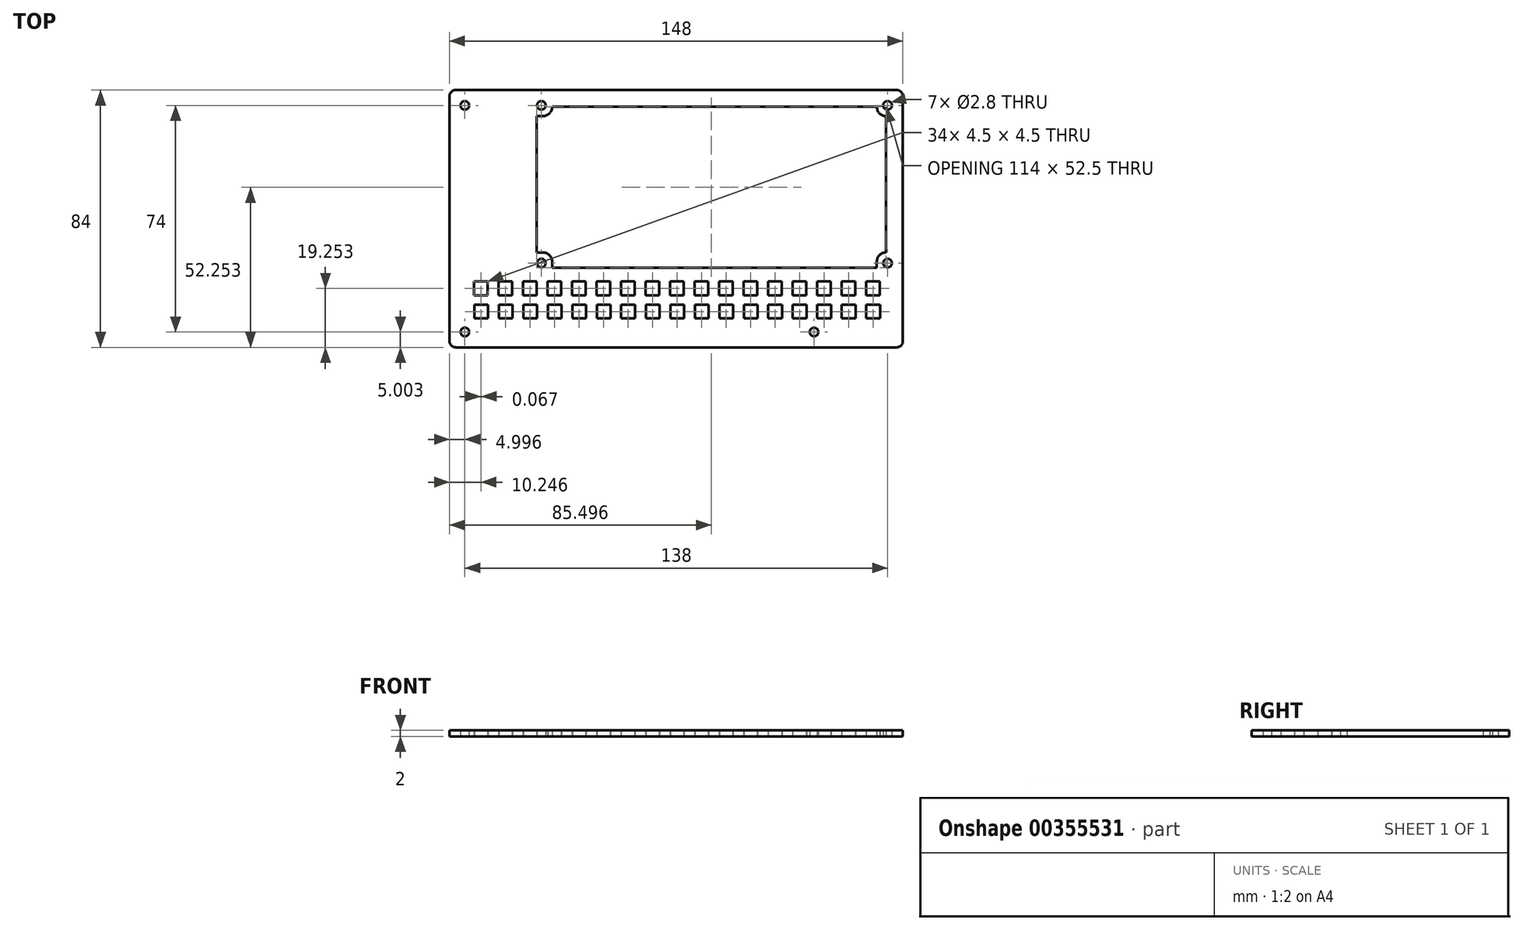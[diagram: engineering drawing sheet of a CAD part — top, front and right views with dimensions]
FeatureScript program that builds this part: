
annotation { "Feature Type Name" : "Feature", "Feature Type Description" : "" }
export const myFeature = defineFeature(function(context is Context, id is Id, definition is map)
    precondition{}
    {
        {
            var Q0;
            Q0=qCreatedBy(makeId("Top.planeOp"),FACE);
            var sketch = newSketch(context, id + "F0", { "sketchPlane" : qUnion([Q0])});
            skLineSegment(sketch, "E0.bottom", {"start": v(-72.45, 22.86) * mm, "end": v(71.55, 22.86) * mm});
            skLineSegment(sketch, "E0.top", {"start": v(-72.45, -61.14) * mm, "end": v(71.55, -61.14) * mm});
            skLineSegment(sketch, "E0.left", {"start": v(-74.45, 20.86) * mm, "end": v(-74.45, -59.14) * mm});
            skLineSegment(sketch, "E0.right", {"start": v(73.55, 20.86) * mm, "end": v(73.55, -59.14) * mm});
            skPoint(sketch, "E1.visualSharp", {"position": v(-74.45, 22.86) * mm});
            skArc(sketch, "E1.filletArc", {"start": v(-72.45, 22.86) * mm, "mid": v(-73.87, 22.28) * mm, "end": v(-74.45, 20.86) * mm});
            skPoint(sketch, "E2.visualSharp", {"position": v(73.55, 22.86) * mm});
            skArc(sketch, "E2.filletArc", {"start": v(73.55, 20.86) * mm, "mid": v(72.96, 22.28) * mm, "end": v(71.55, 22.86) * mm});
            skPoint(sketch, "E3.visualSharp", {"position": v(73.55, -61.14) * mm});
            skArc(sketch, "E3.filletArc", {"start": v(71.55, -61.14) * mm, "mid": v(72.96, -60.55) * mm, "end": v(73.55, -59.14) * mm});
            skPoint(sketch, "E4.visualSharp", {"position": v(-74.45, -61.14) * mm});
            skArc(sketch, "E4.filletArc", {"start": v(-74.45, -59.14) * mm, "mid": v(-73.87, -60.55) * mm, "end": v(-72.45, -61.14) * mm});
            skCircle(sketch, "E5", {"center": v(-69.45, 17.86) * mm, "radius": 1.4 * mm});
            skCircle(sketch, "E6", {"center": v(68.55, 17.86) * mm, "radius": 1.4 * mm});
            skCircle(sketch, "E7", {"center": v(-44.45, 17.86) * mm, "radius": 1.4 * mm});
            skCircle(sketch, "E8", {"center": v(-44.45, -33.64) * mm, "radius": 1.4 * mm});
            skCircle(sketch, "E9", {"center": v(68.55, -33.64) * mm, "radius": 1.4 * mm});
            skCircle(sketch, "E10", {"center": v(-69.45, -56.14) * mm, "radius": 1.4 * mm});
            skCircle(sketch, "E11", {"center": v(44.55, -56.14) * mm, "radius": 1.4 * mm});
            skLineSegment(sketch, "E12.top", {"start": v(-45.95, 14.36) * mm, "end": v(-43.95, 14.36) * mm});
            skLineSegment(sketch, "E13.top", {"start": v(-45.95, -30.14) * mm, "end": v(-43.95, -30.14) * mm});
            skLineSegment(sketch, "E13.right", {"start": v(-40.95, -35.14) * mm, "end": v(-40.95, -33.14) * mm});
            skLineSegment(sketch, "E14.right", {"start": v(65.05, -35.14) * mm, "end": v(65.05, -33.14) * mm});
            skLineSegment(sketch, "E15", {"start": v(65.05, -35.14) * mm, "end": v(-40.95, -35.14) * mm});
            skLineSegment(sketch, "E16", {"start": v(-45.95, -30.14) * mm, "end": v(-45.95, 14.36) * mm});
            skPoint(sketch, "E17.visualSharp", {"position": v(-40.95, 14.36) * mm});
            skArc(sketch, "E17.filletArc", {"start": v(-43.95, 14.36) * mm, "mid": v(-41.83, 15.24) * mm, "end": v(-40.95, 17.36) * mm});
            skPoint(sketch, "E18.visualSharp", {"position": v(65.05, 14.36) * mm});
            skArc(sketch, "E18.filletArc", {"start": v(65.05, 17.36) * mm, "mid": v(65.92, 15.24) * mm, "end": v(68.05, 14.36) * mm});
            skPoint(sketch, "E19.visualSharp", {"position": v(65.05, -30.14) * mm});
            skArc(sketch, "E19.filletArc", {"start": v(68.05, -30.14) * mm, "mid": v(65.92, -31.02) * mm, "end": v(65.05, -33.14) * mm});
            skPoint(sketch, "E20.visualSharp", {"position": v(-40.95, -30.14) * mm});
            skArc(sketch, "E20.filletArc", {"start": v(-40.95, -33.14) * mm, "mid": v(-41.83, -31.02) * mm, "end": v(-43.95, -30.14) * mm});
            skLineSegment(sketch, "E21", {"start": v(68.05, 14.36) * mm, "end": v(68.05, -30.14) * mm});
            skLineSegment(sketch, "E22", {"start": v(65.05, 17.36) * mm, "end": v(-40.95, 17.36) * mm});
            skLineSegment(sketch, "E23.bottom", {"start": v(-66.45, -39.64) * mm, "end": v(-61.95, -39.64) * mm});
            skLineSegment(sketch, "E23.top", {"start": v(-66.45, -44.14) * mm, "end": v(-61.95, -44.14) * mm});
            skLineSegment(sketch, "E23.left", {"start": v(-66.45, -39.64) * mm, "end": v(-66.45, -44.14) * mm});
            skLineSegment(sketch, "E23.right", {"start": v(-61.95, -39.64) * mm, "end": v(-61.95, -44.14) * mm});
            skLineSegment(sketch, "E24.bottom", {"start": v(-66.39, -47.2) * mm, "end": v(-61.89, -47.2) * mm});
            skLineSegment(sketch, "E24.top", {"start": v(-66.39, -51.7) * mm, "end": v(-61.89, -51.7) * mm});
            skLineSegment(sketch, "E24.left", {"start": v(-66.39, -47.2) * mm, "end": v(-66.39, -51.7) * mm});
            skLineSegment(sketch, "E24.right", {"start": v(-61.89, -47.2) * mm, "end": v(-61.89, -51.7) * mm});
            skLineSegment(sketch, "E25.1.0.0", {"start": v(-53.89, -47.2) * mm, "end": v(-53.89, -51.7) * mm});
            skLineSegment(sketch, "E25.1.0.1", {"start": v(-58.39, -47.2) * mm, "end": v(-58.39, -51.7) * mm});
            skLineSegment(sketch, "E25.1.0.2", {"start": v(-58.39, -51.7) * mm, "end": v(-53.89, -51.7) * mm});
            skLineSegment(sketch, "E25.1.0.3", {"start": v(-58.39, -47.2) * mm, "end": v(-53.89, -47.2) * mm});
            skLineSegment(sketch, "E25.1.0.4", {"start": v(-53.95, -39.64) * mm, "end": v(-53.95, -44.14) * mm});
            skLineSegment(sketch, "E25.1.0.5", {"start": v(-58.45, -44.14) * mm, "end": v(-53.95, -44.14) * mm});
            skLineSegment(sketch, "E25.1.0.6", {"start": v(-58.45, -39.64) * mm, "end": v(-58.45, -44.14) * mm});
            skLineSegment(sketch, "E25.1.0.7", {"start": v(-58.45, -39.64) * mm, "end": v(-53.95, -39.64) * mm});
            skLineSegment(sketch, "E25.2.0.0", {"start": v(-45.89, -47.2) * mm, "end": v(-45.89, -51.7) * mm});
            skLineSegment(sketch, "E25.2.0.1", {"start": v(-50.39, -47.2) * mm, "end": v(-50.39, -51.7) * mm});
            skLineSegment(sketch, "E25.2.0.2", {"start": v(-50.39, -51.7) * mm, "end": v(-45.89, -51.7) * mm});
            skLineSegment(sketch, "E25.2.0.3", {"start": v(-50.39, -47.2) * mm, "end": v(-45.89, -47.2) * mm});
            skLineSegment(sketch, "E25.2.0.4", {"start": v(-45.95, -39.64) * mm, "end": v(-45.95, -44.14) * mm});
            skLineSegment(sketch, "E25.2.0.5", {"start": v(-50.45, -44.14) * mm, "end": v(-45.95, -44.14) * mm});
            skLineSegment(sketch, "E25.2.0.6", {"start": v(-50.45, -39.64) * mm, "end": v(-50.45, -44.14) * mm});
            skLineSegment(sketch, "E25.2.0.7", {"start": v(-50.45, -39.64) * mm, "end": v(-45.95, -39.64) * mm});
            skLineSegment(sketch, "E25.3.0.0", {"start": v(-37.89, -47.2) * mm, "end": v(-37.89, -51.7) * mm});
            skLineSegment(sketch, "E25.3.0.1", {"start": v(-42.39, -47.2) * mm, "end": v(-42.39, -51.7) * mm});
            skLineSegment(sketch, "E25.3.0.2", {"start": v(-42.39, -51.7) * mm, "end": v(-37.89, -51.7) * mm});
            skLineSegment(sketch, "E25.3.0.3", {"start": v(-42.39, -47.2) * mm, "end": v(-37.89, -47.2) * mm});
            skLineSegment(sketch, "E25.3.0.4", {"start": v(-37.95, -39.64) * mm, "end": v(-37.95, -44.14) * mm});
            skLineSegment(sketch, "E25.3.0.5", {"start": v(-42.45, -44.14) * mm, "end": v(-37.95, -44.14) * mm});
            skLineSegment(sketch, "E25.3.0.6", {"start": v(-42.45, -39.64) * mm, "end": v(-42.45, -44.14) * mm});
            skLineSegment(sketch, "E25.3.0.7", {"start": v(-42.45, -39.64) * mm, "end": v(-37.95, -39.64) * mm});
            skLineSegment(sketch, "E25.4.0.0", {"start": v(-29.89, -47.2) * mm, "end": v(-29.89, -51.7) * mm});
            skLineSegment(sketch, "E25.4.0.1", {"start": v(-34.39, -47.2) * mm, "end": v(-34.39, -51.7) * mm});
            skLineSegment(sketch, "E25.4.0.2", {"start": v(-34.39, -51.7) * mm, "end": v(-29.89, -51.7) * mm});
            skLineSegment(sketch, "E25.4.0.3", {"start": v(-34.39, -47.2) * mm, "end": v(-29.89, -47.2) * mm});
            skLineSegment(sketch, "E25.4.0.4", {"start": v(-29.95, -39.64) * mm, "end": v(-29.95, -44.14) * mm});
            skLineSegment(sketch, "E25.4.0.5", {"start": v(-34.45, -44.14) * mm, "end": v(-29.95, -44.14) * mm});
            skLineSegment(sketch, "E25.4.0.6", {"start": v(-34.45, -39.64) * mm, "end": v(-34.45, -44.14) * mm});
            skLineSegment(sketch, "E25.4.0.7", {"start": v(-34.45, -39.64) * mm, "end": v(-29.95, -39.64) * mm});
            skLineSegment(sketch, "E25.5.0.0", {"start": v(-21.89, -47.2) * mm, "end": v(-21.89, -51.7) * mm});
            skLineSegment(sketch, "E25.5.0.1", {"start": v(-26.39, -47.2) * mm, "end": v(-26.39, -51.7) * mm});
            skLineSegment(sketch, "E25.5.0.2", {"start": v(-26.39, -51.7) * mm, "end": v(-21.89, -51.7) * mm});
            skLineSegment(sketch, "E25.5.0.3", {"start": v(-26.39, -47.2) * mm, "end": v(-21.89, -47.2) * mm});
            skLineSegment(sketch, "E25.5.0.4", {"start": v(-21.95, -39.64) * mm, "end": v(-21.95, -44.14) * mm});
            skLineSegment(sketch, "E25.5.0.5", {"start": v(-26.45, -44.14) * mm, "end": v(-21.95, -44.14) * mm});
            skLineSegment(sketch, "E25.5.0.6", {"start": v(-26.45, -39.64) * mm, "end": v(-26.45, -44.14) * mm});
            skLineSegment(sketch, "E25.5.0.7", {"start": v(-26.45, -39.64) * mm, "end": v(-21.95, -39.64) * mm});
            skLineSegment(sketch, "E25.6.0.0", {"start": v(-13.89, -47.2) * mm, "end": v(-13.89, -51.7) * mm});
            skLineSegment(sketch, "E25.6.0.1", {"start": v(-18.39, -47.2) * mm, "end": v(-18.39, -51.7) * mm});
            skLineSegment(sketch, "E25.6.0.2", {"start": v(-18.39, -51.7) * mm, "end": v(-13.89, -51.7) * mm});
            skLineSegment(sketch, "E25.6.0.3", {"start": v(-18.39, -47.2) * mm, "end": v(-13.89, -47.2) * mm});
            skLineSegment(sketch, "E25.6.0.4", {"start": v(-13.95, -39.64) * mm, "end": v(-13.95, -44.14) * mm});
            skLineSegment(sketch, "E25.6.0.5", {"start": v(-18.45, -44.14) * mm, "end": v(-13.95, -44.14) * mm});
            skLineSegment(sketch, "E25.6.0.6", {"start": v(-18.45, -39.64) * mm, "end": v(-18.45, -44.14) * mm});
            skLineSegment(sketch, "E25.6.0.7", {"start": v(-18.45, -39.64) * mm, "end": v(-13.95, -39.64) * mm});
            skLineSegment(sketch, "E25.7.0.0", {"start": v(-5.89, -47.2) * mm, "end": v(-5.89, -51.7) * mm});
            skLineSegment(sketch, "E25.7.0.1", {"start": v(-10.39, -47.2) * mm, "end": v(-10.39, -51.7) * mm});
            skLineSegment(sketch, "E25.7.0.2", {"start": v(-10.39, -51.7) * mm, "end": v(-5.89, -51.7) * mm});
            skLineSegment(sketch, "E25.7.0.3", {"start": v(-10.39, -47.2) * mm, "end": v(-5.89, -47.2) * mm});
            skLineSegment(sketch, "E25.7.0.4", {"start": v(-5.95, -39.64) * mm, "end": v(-5.95, -44.14) * mm});
            skLineSegment(sketch, "E25.7.0.5", {"start": v(-10.45, -44.14) * mm, "end": v(-5.95, -44.14) * mm});
            skLineSegment(sketch, "E25.7.0.6", {"start": v(-10.45, -39.64) * mm, "end": v(-10.45, -44.14) * mm});
            skLineSegment(sketch, "E25.7.0.7", {"start": v(-10.45, -39.64) * mm, "end": v(-5.95, -39.64) * mm});
            skLineSegment(sketch, "E25.8.0.0", {"start": v(2.11, -47.2) * mm, "end": v(2.11, -51.7) * mm});
            skLineSegment(sketch, "E25.8.0.1", {"start": v(-2.39, -47.2) * mm, "end": v(-2.39, -51.7) * mm});
            skLineSegment(sketch, "E25.8.0.2", {"start": v(-2.39, -51.7) * mm, "end": v(2.11, -51.7) * mm});
            skLineSegment(sketch, "E25.8.0.3", {"start": v(-2.39, -47.2) * mm, "end": v(2.11, -47.2) * mm});
            skLineSegment(sketch, "E25.8.0.4", {"start": v(2.05, -39.64) * mm, "end": v(2.05, -44.14) * mm});
            skLineSegment(sketch, "E25.8.0.5", {"start": v(-2.45, -44.14) * mm, "end": v(2.05, -44.14) * mm});
            skLineSegment(sketch, "E25.8.0.6", {"start": v(-2.45, -39.64) * mm, "end": v(-2.45, -44.14) * mm});
            skLineSegment(sketch, "E25.8.0.7", {"start": v(-2.45, -39.64) * mm, "end": v(2.05, -39.64) * mm});
            skLineSegment(sketch, "E25.9.0.0", {"start": v(10.11, -47.2) * mm, "end": v(10.11, -51.7) * mm});
            skLineSegment(sketch, "E25.9.0.1", {"start": v(5.61, -47.2) * mm, "end": v(5.61, -51.7) * mm});
            skLineSegment(sketch, "E25.9.0.2", {"start": v(5.61, -51.7) * mm, "end": v(10.11, -51.7) * mm});
            skLineSegment(sketch, "E25.9.0.3", {"start": v(5.61, -47.2) * mm, "end": v(10.11, -47.2) * mm});
            skLineSegment(sketch, "E25.9.0.4", {"start": v(10.05, -39.64) * mm, "end": v(10.05, -44.14) * mm});
            skLineSegment(sketch, "E25.9.0.5", {"start": v(5.55, -44.14) * mm, "end": v(10.05, -44.14) * mm});
            skLineSegment(sketch, "E25.9.0.6", {"start": v(5.55, -39.64) * mm, "end": v(5.55, -44.14) * mm});
            skLineSegment(sketch, "E25.9.0.7", {"start": v(5.55, -39.64) * mm, "end": v(10.05, -39.64) * mm});
            skLineSegment(sketch, "E25.10.0.0", {"start": v(18.11, -47.2) * mm, "end": v(18.11, -51.7) * mm});
            skLineSegment(sketch, "E25.10.0.1", {"start": v(13.61, -47.2) * mm, "end": v(13.61, -51.7) * mm});
            skLineSegment(sketch, "E25.10.0.2", {"start": v(13.61, -51.7) * mm, "end": v(18.11, -51.7) * mm});
            skLineSegment(sketch, "E25.10.0.3", {"start": v(13.61, -47.2) * mm, "end": v(18.11, -47.2) * mm});
            skLineSegment(sketch, "E25.10.0.4", {"start": v(18.05, -39.64) * mm, "end": v(18.05, -44.14) * mm});
            skLineSegment(sketch, "E25.10.0.5", {"start": v(13.55, -44.14) * mm, "end": v(18.05, -44.14) * mm});
            skLineSegment(sketch, "E25.10.0.6", {"start": v(13.55, -39.64) * mm, "end": v(13.55, -44.14) * mm});
            skLineSegment(sketch, "E25.10.0.7", {"start": v(13.55, -39.64) * mm, "end": v(18.05, -39.64) * mm});
            skLineSegment(sketch, "E25.11.0.0", {"start": v(26.11, -47.2) * mm, "end": v(26.11, -51.7) * mm});
            skLineSegment(sketch, "E25.11.0.1", {"start": v(21.61, -47.2) * mm, "end": v(21.61, -51.7) * mm});
            skLineSegment(sketch, "E25.11.0.2", {"start": v(21.61, -51.7) * mm, "end": v(26.11, -51.7) * mm});
            skLineSegment(sketch, "E25.11.0.3", {"start": v(21.61, -47.2) * mm, "end": v(26.11, -47.2) * mm});
            skLineSegment(sketch, "E25.11.0.4", {"start": v(26.05, -39.64) * mm, "end": v(26.05, -44.14) * mm});
            skLineSegment(sketch, "E25.11.0.5", {"start": v(21.55, -44.14) * mm, "end": v(26.05, -44.14) * mm});
            skLineSegment(sketch, "E25.11.0.6", {"start": v(21.55, -39.64) * mm, "end": v(21.55, -44.14) * mm});
            skLineSegment(sketch, "E25.11.0.7", {"start": v(21.55, -39.64) * mm, "end": v(26.05, -39.64) * mm});
            skLineSegment(sketch, "E25.12.0.0", {"start": v(34.11, -47.2) * mm, "end": v(34.11, -51.7) * mm});
            skLineSegment(sketch, "E25.12.0.1", {"start": v(29.61, -47.2) * mm, "end": v(29.61, -51.7) * mm});
            skLineSegment(sketch, "E25.12.0.2", {"start": v(29.61, -51.7) * mm, "end": v(34.11, -51.7) * mm});
            skLineSegment(sketch, "E25.12.0.3", {"start": v(29.61, -47.2) * mm, "end": v(34.11, -47.2) * mm});
            skLineSegment(sketch, "E25.12.0.4", {"start": v(34.05, -39.64) * mm, "end": v(34.05, -44.14) * mm});
            skLineSegment(sketch, "E25.12.0.5", {"start": v(29.55, -44.14) * mm, "end": v(34.05, -44.14) * mm});
            skLineSegment(sketch, "E25.12.0.6", {"start": v(29.55, -39.64) * mm, "end": v(29.55, -44.14) * mm});
            skLineSegment(sketch, "E25.12.0.7", {"start": v(29.55, -39.64) * mm, "end": v(34.05, -39.64) * mm});
            skLineSegment(sketch, "E25.13.0.0", {"start": v(42.11, -47.2) * mm, "end": v(42.11, -51.7) * mm});
            skLineSegment(sketch, "E25.13.0.1", {"start": v(37.61, -47.2) * mm, "end": v(37.61, -51.7) * mm});
            skLineSegment(sketch, "E25.13.0.2", {"start": v(37.61, -51.7) * mm, "end": v(42.11, -51.7) * mm});
            skLineSegment(sketch, "E25.13.0.3", {"start": v(37.61, -47.2) * mm, "end": v(42.11, -47.2) * mm});
            skLineSegment(sketch, "E25.13.0.4", {"start": v(42.05, -39.64) * mm, "end": v(42.05, -44.14) * mm});
            skLineSegment(sketch, "E25.13.0.5", {"start": v(37.55, -44.14) * mm, "end": v(42.05, -44.14) * mm});
            skLineSegment(sketch, "E25.13.0.6", {"start": v(37.55, -39.64) * mm, "end": v(37.55, -44.14) * mm});
            skLineSegment(sketch, "E25.13.0.7", {"start": v(37.55, -39.64) * mm, "end": v(42.05, -39.64) * mm});
            skLineSegment(sketch, "E25.14.0.0", {"start": v(50.11, -47.2) * mm, "end": v(50.11, -51.7) * mm});
            skLineSegment(sketch, "E25.14.0.1", {"start": v(45.61, -47.2) * mm, "end": v(45.61, -51.7) * mm});
            skLineSegment(sketch, "E25.14.0.2", {"start": v(45.61, -51.7) * mm, "end": v(50.11, -51.7) * mm});
            skLineSegment(sketch, "E25.14.0.3", {"start": v(45.61, -47.2) * mm, "end": v(50.11, -47.2) * mm});
            skLineSegment(sketch, "E25.14.0.4", {"start": v(50.05, -39.64) * mm, "end": v(50.05, -44.14) * mm});
            skLineSegment(sketch, "E25.14.0.5", {"start": v(45.55, -44.14) * mm, "end": v(50.05, -44.14) * mm});
            skLineSegment(sketch, "E25.14.0.6", {"start": v(45.55, -39.64) * mm, "end": v(45.55, -44.14) * mm});
            skLineSegment(sketch, "E25.14.0.7", {"start": v(45.55, -39.64) * mm, "end": v(50.05, -39.64) * mm});
            skLineSegment(sketch, "E25.15.0.0", {"start": v(58.11, -47.2) * mm, "end": v(58.11, -51.7) * mm});
            skLineSegment(sketch, "E25.15.0.1", {"start": v(53.61, -47.2) * mm, "end": v(53.61, -51.7) * mm});
            skLineSegment(sketch, "E25.15.0.2", {"start": v(53.61, -51.7) * mm, "end": v(58.11, -51.7) * mm});
            skLineSegment(sketch, "E25.15.0.3", {"start": v(53.61, -47.2) * mm, "end": v(58.11, -47.2) * mm});
            skLineSegment(sketch, "E25.15.0.4", {"start": v(58.05, -39.64) * mm, "end": v(58.05, -44.14) * mm});
            skLineSegment(sketch, "E25.15.0.5", {"start": v(53.55, -44.14) * mm, "end": v(58.05, -44.14) * mm});
            skLineSegment(sketch, "E25.15.0.6", {"start": v(53.55, -39.64) * mm, "end": v(53.55, -44.14) * mm});
            skLineSegment(sketch, "E25.15.0.7", {"start": v(53.55, -39.64) * mm, "end": v(58.05, -39.64) * mm});
            skLineSegment(sketch, "E25.16.0.0", {"start": v(66.11, -47.2) * mm, "end": v(66.11, -51.7) * mm});
            skLineSegment(sketch, "E25.16.0.1", {"start": v(61.61, -47.2) * mm, "end": v(61.61, -51.7) * mm});
            skLineSegment(sketch, "E25.16.0.2", {"start": v(61.61, -51.7) * mm, "end": v(66.11, -51.7) * mm});
            skLineSegment(sketch, "E25.16.0.3", {"start": v(61.61, -47.2) * mm, "end": v(66.11, -47.2) * mm});
            skLineSegment(sketch, "E25.16.0.4", {"start": v(66.05, -39.64) * mm, "end": v(66.05, -44.14) * mm});
            skLineSegment(sketch, "E25.16.0.5", {"start": v(61.55, -44.14) * mm, "end": v(66.05, -44.14) * mm});
            skLineSegment(sketch, "E25.16.0.6", {"start": v(61.55, -39.64) * mm, "end": v(61.55, -44.14) * mm});
            skLineSegment(sketch, "E25.16.0.7", {"start": v(61.55, -39.64) * mm, "end": v(66.05, -39.64) * mm});
            skLineSegment(sketch, "E25.direction1", {"start": v(-66.39, -51.7) * mm, "end": v(-58.39, -51.7) * mm, "construction": true});
            skSolve(sketch);
        }
        {
            var Q0;
            Q0=makeQuery(id+"F0.imprint","IMPRINT",FACE,{"disambiguationData":[TD([[makeQuery(id+"F0.imprint","IMPRINT",EDGE,{"derivedFrom":sQuery(id+"F0.wireOp",EDGE,"E0.bottom")}),-1.0]])]});
            extrude(context, id + "F1", {"entities" : qUnion([Q0]), "depth" : 2 * mm});
        }
    });
